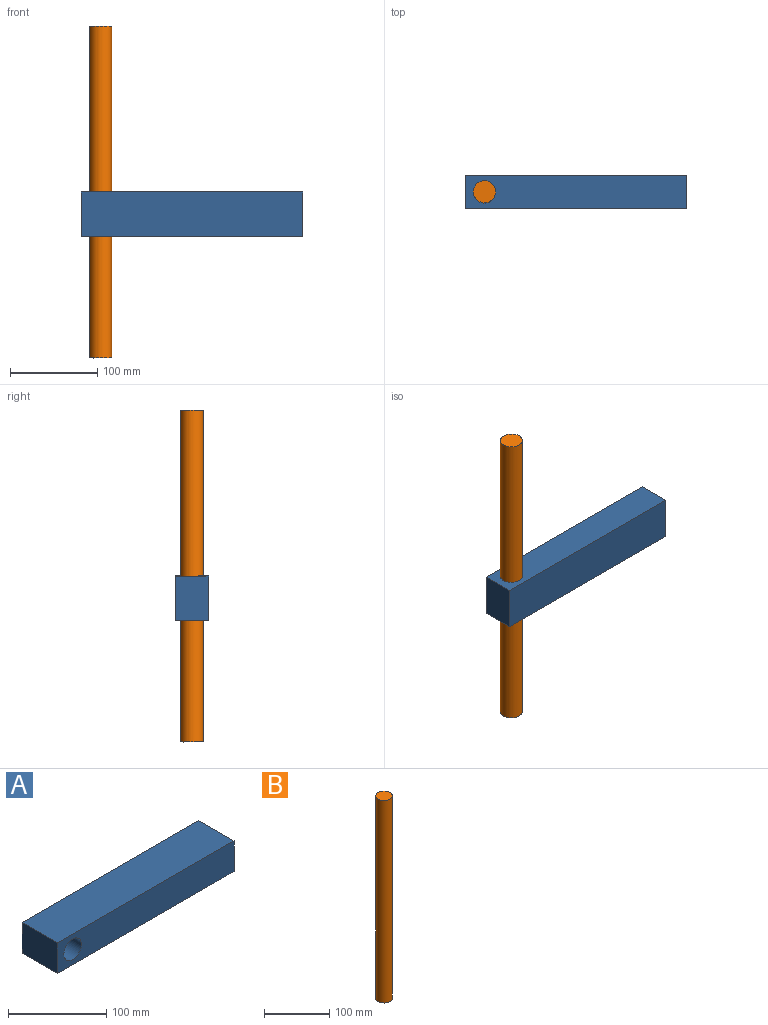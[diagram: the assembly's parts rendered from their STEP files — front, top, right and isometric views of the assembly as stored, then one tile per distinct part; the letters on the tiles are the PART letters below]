
ASSEMBLY  parts=2 mates=1
PART A: 7 faces, bbox 254x50.8x38.1 mm
  f0: plane 50.8x38.1mm, normal (-1,0,0), area 1935.5mm2, adj f1,f3,f4,f5
  f1: plane 254x38.1mm, normal (0,-1,0), area 9170.7mm2, adj f0,f2,f4,f5,f6
  f2: plane 50.8x38.1mm, normal (1,0,0), area 1935.5mm2, adj f1,f3,f4,f5
  f3: plane 254x38.1mm, normal (0,1,0), area 9170.7mm2, adj f0,f2,f4,f5,f6
  f4: plane 254x50.8mm, normal (0,0,1), area 12903.2mm2, adj f0,f1,f2,f3
  f5: plane 254x50.8mm, normal (0,0,-1), area 12903.2mm2, adj f0,f1,f2,f3
  f6: cylinder r=12.7mm len=50.8mm, axis (0,1,0), area 4053.7mm2, adj f1,f3
PART B: 3 faces, bbox 25.4x25.4x381 mm
  f0: cylinder r=12.7mm len=381mm, axis (0,0,-1), area 30402.4mm2, adj f1,f2
  f1: plane 25.4x25.4mm, normal (0,0,1), area 506.7mm2, adj f0
  f2: plane 25.4x25.4mm, normal (0,0,-1), area 506.7mm2, adj f0
PLACE A rot(axis=(-1,0,0),90deg) t=(120.25,-50.91,19.49)mm
PLACE B t=(142.28,-31.86,-171.01)mm
MATE fastened A.f6 <-> B.f0  axis (0,0,-1) through (142.28,-31.86,19.49)mm
